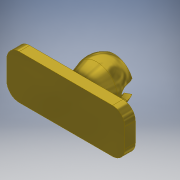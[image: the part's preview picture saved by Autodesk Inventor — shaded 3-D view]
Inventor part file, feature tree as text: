
AUTODESK INVENTOR PART (.ipt)
format: ipt  version: 2018.1 (Build 221151000, 151)  size: 198,656 bytes
history: native  units: in
note: dims shown in document units (in); Inventor stores cm internally (conversion verified against a paired STEP export)
features: sketch x8, extrude x4, revolve x4, plane x3
ambient origin geometry x8: Origin, YZ Plane, XZ Plane, XY Plane, X Axis, Y Axis, Z Axis, Center Point
bodies: Solid2 (feature_tree)
feature tree (19):
  extrude  "Extrusion1"  Depth=0.535in
  plane  "Work Plane1"
  revolve  "Revolution1"  [1 undecoded]
  extrude  "Extrusion4"  TaperAngle=90.0deg  [1 undecoded]
  revolve  "Revolution2"  Angle=90.0deg
  plane  "Work Plane3"
  revolve  "Revolution3"  [1 undecoded]
  extrude  "Extrusion2"  Depth=0.0395in
  plane  "Work Plane4"
  revolve  "Revolution4"  [1 undecoded]
  extrude  "Extrusion3"  Depth=0.0985in
  sketch  "Sketch1"  dims[d1=0.15in d2=0.0in d8=0.535in]
  sketch  "Sketch2"  dims[d9=0.315in d10=0.2095in]
  sketch  "Sketch4"  dims[d11=90.0deg d12=90.0deg]
  sketch  "Sketch5"  dims[d13=0.472in d14=90.0deg]
  sketch  "Sketch6"  dims[d15=0.541in d16=0.0in d17=0.0in]
  sketch  "Sketch8"  dims[d20=30.0deg d21=0.0395in]
  sketch  "Sketch10"  dims[d22=90.0deg d25=0.197in]
  sketch  "Sketch11"  dims[d27=0.0985in d28=0.113in d29=0.15in d30=0.0in d31=30.0deg d32=30.0deg d33=0.235in d34=0.235in d35=0.118in d36=0.0in]
note: 4 required parameter values undecoded (feature->parameter linkage not recoverable at this tier; creation-order binding heuristic only, values carry confidence <= 0.55)